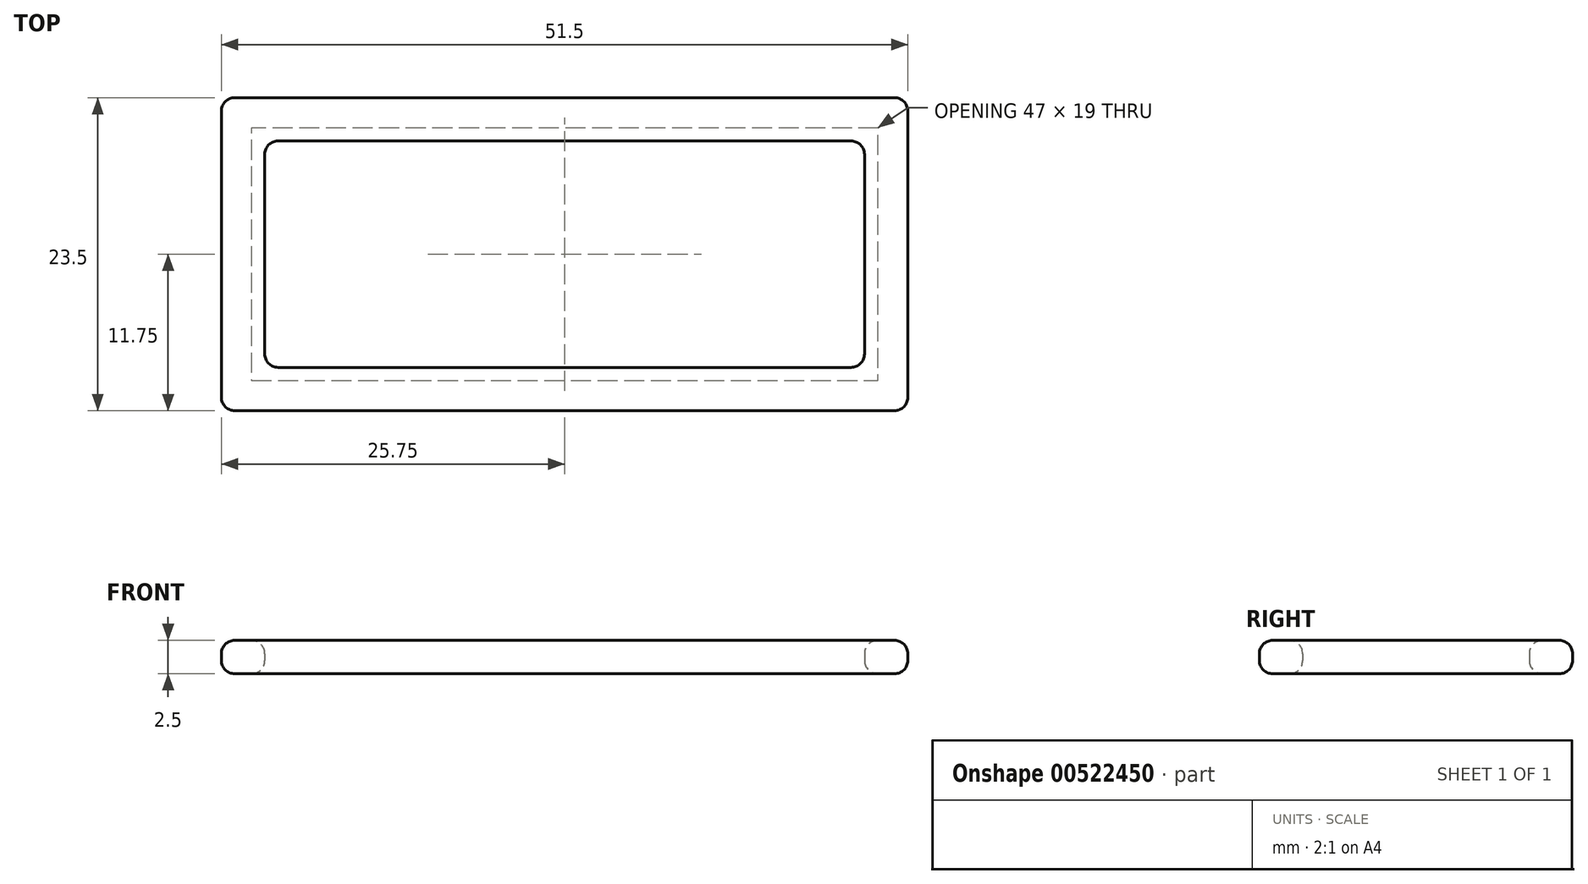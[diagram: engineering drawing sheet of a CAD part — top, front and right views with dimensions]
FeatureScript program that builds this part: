
annotation { "Feature Type Name" : "Feature", "Feature Type Description" : "" }
export const myFeature = defineFeature(function(context is Context, id is Id, definition is map)
    precondition{}
    {
        {
            var Q0;
            Q0=qCreatedBy(makeId("Top.planeOp"),FACE);
            var sketch = newSketch(context, id + "F0", { "sketchPlane" : qUnion([Q0])});
            skLineSegment(sketch, "E0.bottom", {"start": v(0, 0) * mm, "end": v(51.5, 0) * mm});
            skLineSegment(sketch, "E0.top", {"start": v(0, -23.5) * mm, "end": v(51.5, -23.5) * mm});
            skLineSegment(sketch, "E0.left", {"start": v(0, 0) * mm, "end": v(0, -23.5) * mm});
            skLineSegment(sketch, "E0.right", {"start": v(51.5, 0) * mm, "end": v(51.5, -23.5) * mm});
            skLineSegment(sketch, "E1.bottom", {"start": v(3.25, -3.25) * mm, "end": v(48.25, -3.25) * mm});
            skLineSegment(sketch, "E1.top", {"start": v(3.25, -20.25) * mm, "end": v(48.25, -20.25) * mm});
            skLineSegment(sketch, "E1.left", {"start": v(3.25, -3.25) * mm, "end": v(3.25, -20.25) * mm});
            skLineSegment(sketch, "E1.right", {"start": v(48.25, -3.25) * mm, "end": v(48.25, -20.25) * mm});
            skSolve(sketch);
        }
        {
            var Q0;
            Q0=makeQuery(id+"F0.imprint","IMPRINT",FACE,{"disambiguationData":[TD([[makeQuery(id+"F0.imprint","IMPRINT",EDGE,{"derivedFrom":sQuery(id+"F0.wireOp",EDGE,"E0.bottom")}),-1.0]])]});
            extrude(context, id + "F1", {"entities" : qUnion([Q0]), "depth" : 2.5 * mm, "offsetDistance" : 25 * mm});
        }
        {
            var Q0;
            Q0=makeQuery(id+"F1.opExtrude","CAP_EDGE",EDGE,{"disambiguationData":[OSD([sQuery(id+"F0.wireOp",EDGE,"E0.top")])],"isStart":false});
            var Q1;
            Q1=makeQuery(id+"F1.opExtrude","CAP_EDGE",EDGE,{"disambiguationData":[OSD([sQuery(id+"F0.wireOp",EDGE,"E0.top")])],"isStart":true});
            var Q2;
            Q2=makeQuery(id+"F1.opExtrude","SWEPT_EDGE",EDGE,{"disambiguationData":[OSD([sQuery(id+"F0.wireOp",EDGE,"E0.top"),sQuery(id+"F0.wireOp",EDGE,"E0.right")])]});
            var Q3;
            Q3=makeQuery(id+"F1.opExtrude","CAP_EDGE",EDGE,{"disambiguationData":[OSD([sQuery(id+"F0.wireOp",EDGE,"E0.right")])],"isStart":false});
            var Q4;
            Q4=makeQuery(id+"F1.opExtrude","CAP_EDGE",EDGE,{"disambiguationData":[OSD([sQuery(id+"F0.wireOp",EDGE,"E0.right")])],"isStart":true});
            var Q5;
            Q5=makeQuery(id+"F1.opExtrude","CAP_EDGE",EDGE,{"disambiguationData":[OSD([sQuery(id+"F0.wireOp",EDGE,"E1.right")])],"isStart":false});
            var Q6;
            Q6=makeQuery(id+"F1.opExtrude","CAP_EDGE",EDGE,{"disambiguationData":[OSD([sQuery(id+"F0.wireOp",EDGE,"E1.bottom")])],"isStart":false});
            var Q7;
            Q7=makeQuery(id+"F1.opExtrude","CAP_EDGE",EDGE,{"disambiguationData":[OSD([sQuery(id+"F0.wireOp",EDGE,"E1.left")])],"isStart":false});
            var Q8;
            Q8=makeQuery(id+"F1.opExtrude","CAP_EDGE",EDGE,{"disambiguationData":[OSD([sQuery(id+"F0.wireOp",EDGE,"E1.top")])],"isStart":false});
            var Q9;
            Q9=makeQuery(id+"F1.opExtrude","CAP_EDGE",EDGE,{"disambiguationData":[OSD([sQuery(id+"F0.wireOp",EDGE,"E0.bottom")])],"isStart":false});
            var Q10;
            Q10=makeQuery(id+"F1.opExtrude","CAP_EDGE",EDGE,{"disambiguationData":[OSD([sQuery(id+"F0.wireOp",EDGE,"E0.left")])],"isStart":false});
            var Q11;
            Q11=makeQuery(id+"F1.opExtrude","SWEPT_EDGE",EDGE,{"disambiguationData":[OSD([sQuery(id+"F0.wireOp",EDGE,"E0.bottom"),sQuery(id+"F0.wireOp",EDGE,"E0.right")])]});
            var Q12;
            Q12=makeQuery(id+"F1.opExtrude","CAP_EDGE",EDGE,{"disambiguationData":[OSD([sQuery(id+"F0.wireOp",EDGE,"E0.bottom")])],"isStart":true});
            var Q13;
            Q13=makeQuery(id+"F1.opExtrude","SWEPT_EDGE",EDGE,{"disambiguationData":[OSD([sQuery(id+"F0.wireOp",EDGE,"E0.bottom"),sQuery(id+"F0.wireOp",EDGE,"E0.left")])]});
            var Q14;
            Q14=makeQuery(id+"F1.opExtrude","SWEPT_EDGE",EDGE,{"disambiguationData":[OSD([sQuery(id+"F0.wireOp",EDGE,"E1.top"),sQuery(id+"F0.wireOp",EDGE,"E1.left")])]});
            var Q15;
            Q15=makeQuery(id+"F1.opExtrude","CAP_EDGE",EDGE,{"disambiguationData":[OSD([sQuery(id+"F0.wireOp",EDGE,"E1.top")])],"isStart":true});
            var Q16;
            Q16=makeQuery(id+"F1.opExtrude","SWEPT_EDGE",EDGE,{"disambiguationData":[OSD([sQuery(id+"F0.wireOp",EDGE,"E1.bottom"),sQuery(id+"F0.wireOp",EDGE,"E1.left")])]});
            var Q17;
            Q17=makeQuery(id+"F1.opExtrude","CAP_EDGE",EDGE,{"disambiguationData":[OSD([sQuery(id+"F0.wireOp",EDGE,"E1.left")])],"isStart":true});
            var Q18;
            Q18=makeQuery(id+"F1.opExtrude","CAP_EDGE",EDGE,{"disambiguationData":[OSD([sQuery(id+"F0.wireOp",EDGE,"E1.bottom")])],"isStart":true});
            var Q19;
            Q19=makeQuery(id+"F1.opExtrude","CAP_EDGE",EDGE,{"disambiguationData":[OSD([sQuery(id+"F0.wireOp",EDGE,"E1.right")])],"isStart":true});
            var Q20;
            Q20=makeQuery(id+"F1.opExtrude","SWEPT_EDGE",EDGE,{"disambiguationData":[OSD([sQuery(id+"F0.wireOp",EDGE,"E1.bottom"),sQuery(id+"F0.wireOp",EDGE,"E1.right")])]});
            var Q21;
            Q21=makeQuery(id+"F1.opExtrude","SWEPT_EDGE",EDGE,{"disambiguationData":[OSD([sQuery(id+"F0.wireOp",EDGE,"E1.top"),sQuery(id+"F0.wireOp",EDGE,"E1.right")])]});
            var Q22;
            Q22=makeQuery(id+"F1.opExtrude","CAP_EDGE",EDGE,{"disambiguationData":[OSD([sQuery(id+"F0.wireOp",EDGE,"E0.left")])],"isStart":true});
            var Q23;
            Q23=makeQuery(id+"F1.opExtrude","SWEPT_EDGE",EDGE,{"disambiguationData":[OSD([sQuery(id+"F0.wireOp",EDGE,"E0.top"),sQuery(id+"F0.wireOp",EDGE,"E0.left")])]});
            fillet(context, id + "F2", {"entities" : qUnion([Q0, Q1, Q2, Q3, Q4, Q5, Q6, Q7, Q8, Q9, Q10, Q11, Q12, Q13, Q14, Q15, Q16, Q17, Q18, Q19, Q20, Q21, Q22, Q23]), "radius" : 1 * mm, "tangentPropagation" : true, "allowEdgeOverflow" : false});
        }
    });
